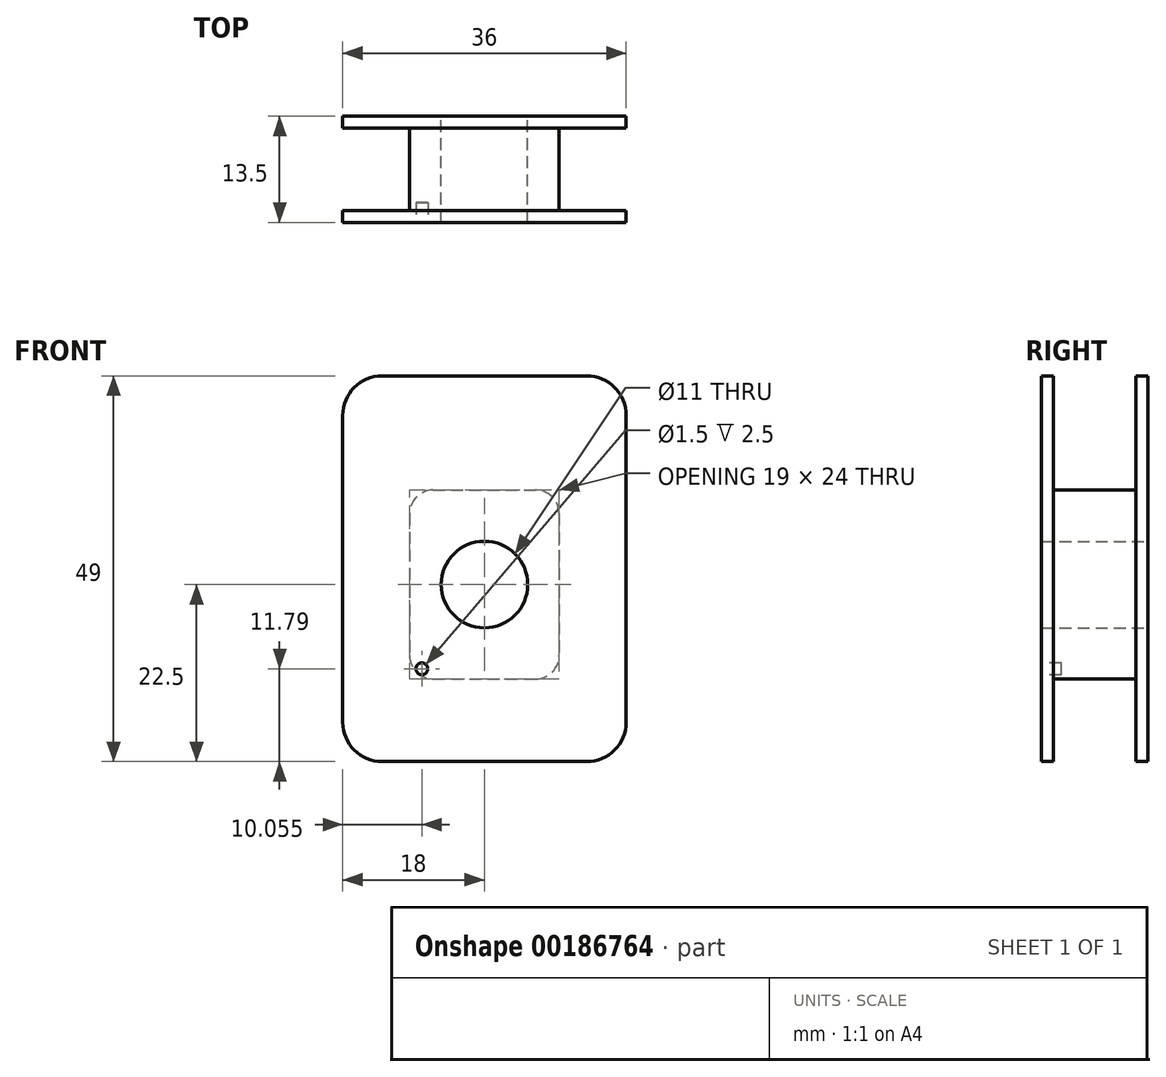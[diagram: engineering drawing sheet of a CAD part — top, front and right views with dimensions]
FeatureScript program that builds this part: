
annotation { "Feature Type Name" : "Feature", "Feature Type Description" : "" }
export const myFeature = defineFeature(function(context is Context, id is Id, definition is map)
    precondition{}
    {
        {
            var Q0;
            Q0=qCreatedBy(makeId("Front.planeOp"),FACE);
            var sketch = newSketch(context, id + "F0", { "sketchPlane" : qUnion([Q0])});
            skLineSegment(sketch, "E0.bottom", {"start": v(-18, 22.5) * mm, "end": v(18, 22.5) * mm});
            skLineSegment(sketch, "E0.top", {"start": v(-18, -22.5) * mm, "end": v(18, -22.5) * mm});
            skLineSegment(sketch, "E0.left", {"start": v(-18, 22.5) * mm, "end": v(-18, -22.5) * mm});
            skLineSegment(sketch, "E0.right", {"start": v(18, 22.5) * mm, "end": v(18, -22.5) * mm});
            skPoint(sketch, "E0.middle", {"position": v(0, 0) * mm});
            skCircle(sketch, "E1", {"center": v(0, 0) * mm, "radius": 5.5 * mm});
            skSolve(sketch);
        }
        {
            var Q0;
            Q0=makeQuery(id+"F0.imprint","IMPRINT",FACE,{"disambiguationData":[TD([[makeQuery(id+"F0.imprint","IMPRINT",EDGE,{"derivedFrom":sQuery(id+"F0.wireOp",EDGE,"E0.bottom")}),-1.0]])]});
            extrude(context, id + "F1", {"entities" : qUnion([Q0]), "depth" : 1.5 * mm});
        }
        {
            var Q0;
            Q0=makeQuery(id+"F1.opExtrude","CAP_FACE",FACE,{"disambiguationData":[OSD([sQuery(id+"F0.wireOp",EDGE,"E0.bottom"),sQuery(id+"F0.wireOp",EDGE,"E0.top"),sQuery(id+"F0.wireOp",EDGE,"E0.left"),sQuery(id+"F0.wireOp",EDGE,"E0.right"),sQuery(id+"F0.wireOp",EDGE,"E1")])],"isStart":false});
            var sketch = newSketch(context, id + "F2", { "sketchPlane" : qUnion([Q0])});
            skLineSegment(sketch, "E2.bottom", {"start": v(-9.5, 12) * mm, "end": v(9.5, 12) * mm});
            skLineSegment(sketch, "E2.top", {"start": v(-9.5, -12) * mm, "end": v(9.5, -12) * mm});
            skLineSegment(sketch, "E2.left", {"start": v(-9.5, 12) * mm, "end": v(-9.5, -12) * mm});
            skLineSegment(sketch, "E2.right", {"start": v(9.5, 12) * mm, "end": v(9.5, -12) * mm});
            skPoint(sketch, "E2.middle", {"position": v(0, 0) * mm});
            skSolve(sketch);
        }
        {
            var Q0;
            Q0=makeQuery(id+"F2.imprint","IMPRINT",FACE,{"disambiguationData":[TD([[makeQuery(id+"F2.imprint","IMPRINT",EDGE,{"derivedFrom":sQuery(id+"F2.wireOp",EDGE,"E2.bottom")}),-1.0]])]});
            extrude(context, id + "F3", {"entities" : qUnion([Q0]), "operationType" : NewBodyOperationType.ADD, "depth" : 12 * mm});
        }
        {
            var Q0;
            Q0=makeQuery(id+"F3.opExtrude","CAP_FACE",FACE,{"disambiguationData":[OSD([sQuery(id+"F0.wireOp",EDGE,"E1"),sQuery(id+"F2.wireOp",EDGE,"E2.bottom"),sQuery(id+"F2.wireOp",EDGE,"E2.top"),sQuery(id+"F2.wireOp",EDGE,"E2.left"),sQuery(id+"F2.wireOp",EDGE,"E2.right")])],"isStart":false});
            var sketch = newSketch(context, id + "F4", { "sketchPlane" : qUnion([Q0])});
            skLineSegment(sketch, "E3.bottom", {"start": v(-18, 22.5) * mm, "end": v(18, 22.5) * mm});
            skLineSegment(sketch, "E3.top", {"start": v(-18, -22.5) * mm, "end": v(18, -22.5) * mm});
            skLineSegment(sketch, "E3.left", {"start": v(-18, 22.5) * mm, "end": v(-18, -22.5) * mm});
            skLineSegment(sketch, "E3.right", {"start": v(18, 22.5) * mm, "end": v(18, -22.5) * mm});
            skPoint(sketch, "E3.middle", {"position": v(0, 0) * mm});
            skSolve(sketch);
        }
        {
            var Q0;
            Q0=makeQuery(id+"F4.imprint","IMPRINT",FACE,{"disambiguationData":[TD([[makeQuery(id+"F4.imprint","IMPRINT",EDGE,{"derivedFrom":sQuery(id+"F4.wireOp",EDGE,"E3.bottom")}),-1.0]])]});
            var Q1;
            Q1=makeQuery(id+"F4.imprint","IMPRINT",FACE,{"disambiguationData":[TD([[makeQuery(id+"F4.imprint","IMPRINT",EDGE,{"derivedFrom":makeQuery(id+"F3.opExtrude","CAP_EDGE",EDGE,{"disambiguationData":[OSD([sQuery(id+"F2.wireOp",EDGE,"E2.bottom")])],"isStart":false})}),-1.0]])]});
            extrude(context, id + "F5", {"entities" : qUnion([Q0, Q1]), "operationType" : NewBodyOperationType.ADD, "oppositeDirection" : true, "depth" : 1.5 * mm});
        }
        {
            var Q0;
            {var subQ0=sQuery(id+"F0.wireOp",EDGE,"E1");Q0=makeQuery(id+"F5.boolean.opBoolean","MERGE",FACE,{"derivedFrom":[makeQuery(id+"F3.opExtrude","CAP_FACE",FACE,{"disambiguationData":[OSD([subQ0,sQuery(id+"F2.wireOp",EDGE,"E2.bottom"),sQuery(id+"F2.wireOp",EDGE,"E2.top"),sQuery(id+"F2.wireOp",EDGE,"E2.left"),sQuery(id+"F2.wireOp",EDGE,"E2.right")])],"isStart":false}),makeQuery(id+"F5.opExtrude","CAP_FACE",FACE,{"disambiguationData":[OSD([subQ0,sQuery(id+"F4.wireOp",EDGE,"E3.bottom"),sQuery(id+"F4.wireOp",EDGE,"E3.top"),sQuery(id+"F4.wireOp",EDGE,"E3.left"),sQuery(id+"F4.wireOp",EDGE,"E3.right")])],"isStart":true})]});}
            var sketch = newSketch(context, id + "F6", { "sketchPlane" : qUnion([Q0])});
            skCircle(sketch, "E4", {"center": v(-7.94, -10.71) * mm, "radius": 0.75 * mm});
            skPoint(sketch, "E5.middle", {"position": v(0, 0) * mm});
            skSolve(sketch);
        }
        {
            var Q0;
            Q0=makeQuery(id+"F6.imprint","IMPRINT",FACE,{"disambiguationData":[TD([[makeQuery(id+"F6.imprint","IMPRINT",EDGE,{"derivedFrom":sQuery(id+"F6.wireOp",EDGE,"E4")}),1.0]])]});
            extrude(context, id + "F7", {"entities" : qUnion([Q0]), "operationType" : NewBodyOperationType.REMOVE, "oppositeDirection" : true, "depth" : 2.5 * mm});
        }
        {
            var Q0;
            {var subQ0=sQuery(id+"F0.wireOp",EDGE,"E1");Q0=makeQuery(id+"F5.boolean.opBoolean","MERGE",FACE,{"derivedFrom":[makeQuery(id+"F3.opExtrude","CAP_FACE",FACE,{"disambiguationData":[OSD([subQ0,sQuery(id+"F2.wireOp",EDGE,"E2.bottom"),sQuery(id+"F2.wireOp",EDGE,"E2.top"),sQuery(id+"F2.wireOp",EDGE,"E2.left"),sQuery(id+"F2.wireOp",EDGE,"E2.right")])],"isStart":false}),makeQuery(id+"F5.opExtrude","CAP_FACE",FACE,{"disambiguationData":[OSD([subQ0,sQuery(id+"F4.wireOp",EDGE,"E3.bottom"),sQuery(id+"F4.wireOp",EDGE,"E3.top"),sQuery(id+"F4.wireOp",EDGE,"E3.left"),sQuery(id+"F4.wireOp",EDGE,"E3.right")])],"isStart":true})]});}
            var sketch = newSketch(context, id + "F8", { "sketchPlane" : qUnion([Q0])});
            skLineSegment(sketch, "E6.bottom", {"start": v(-18, 22.5) * mm, "end": v(18, 22.5) * mm});
            skLineSegment(sketch, "E6.top", {"start": v(-18, 26.5) * mm, "end": v(18, 26.5) * mm});
            skLineSegment(sketch, "E6.left", {"start": v(-18, 22.5) * mm, "end": v(-18, 26.5) * mm});
            skLineSegment(sketch, "E6.right", {"start": v(18, 22.5) * mm, "end": v(18, 26.5) * mm});
            skSolve(sketch);
        }
        {
            var Q0;
            Q0=makeQuery(id+"F8.imprint","IMPRINT",FACE,{"disambiguationData":[TD([[makeQuery(id+"F8.imprint","IMPRINT",EDGE,{"derivedFrom":sQuery(id+"F8.wireOp",EDGE,"E6.bottom")}),1.0]])]});
            extrude(context, id + "F9", {"entities" : qUnion([Q0]), "operationType" : NewBodyOperationType.ADD, "oppositeDirection" : true, "depth" : 1.5 * mm});
        }
        {
            var Q0;
            Q0=makeQuery(id+"F1.opExtrude","CAP_FACE",FACE,{"disambiguationData":[OSD([sQuery(id+"F0.wireOp",EDGE,"E0.bottom"),sQuery(id+"F0.wireOp",EDGE,"E0.top"),sQuery(id+"F0.wireOp",EDGE,"E0.left"),sQuery(id+"F0.wireOp",EDGE,"E0.right"),sQuery(id+"F0.wireOp",EDGE,"E1")])],"isStart":true});
            var sketch = newSketch(context, id + "F10", { "sketchPlane" : qUnion([Q0])});
            skLineSegment(sketch, "E7.bottom", {"start": v(-18, 22.5) * mm, "end": v(18, 22.5) * mm});
            skLineSegment(sketch, "E7.top", {"start": v(-18, 26.5) * mm, "end": v(18, 26.5) * mm});
            skLineSegment(sketch, "E7.left", {"start": v(-18, 22.5) * mm, "end": v(-18, 26.5) * mm});
            skLineSegment(sketch, "E7.right", {"start": v(18, 22.5) * mm, "end": v(18, 26.5) * mm});
            skSolve(sketch);
        }
        {
            var Q0;
            Q0=makeQuery(id+"F10.imprint","IMPRINT",FACE,{"disambiguationData":[TD([[makeQuery(id+"F10.imprint","IMPRINT",EDGE,{"derivedFrom":sQuery(id+"F10.wireOp",EDGE,"E7.bottom")}),-1.0]])]});
            extrude(context, id + "F11", {"entities" : qUnion([Q0]), "operationType" : NewBodyOperationType.ADD, "oppositeDirection" : true, "depth" : 1.5 * mm});
        }
        {
            var Q0;
            Q0=makeQuery(id+"F9.opExtrude","SWEPT_EDGE",EDGE,{"disambiguationData":[OSD([sQuery(id+"F8.wireOp",EDGE,"E6.top"),sQuery(id+"F8.wireOp",EDGE,"E6.right")])]});
            var Q1;
            Q1=makeQuery(id+"F11.opExtrude","SWEPT_EDGE",EDGE,{"disambiguationData":[OSD([sQuery(id+"F10.wireOp",EDGE,"E7.top"),sQuery(id+"F10.wireOp",EDGE,"E7.left")])]});
            var Q2;
            Q2=makeQuery(id+"F1.opExtrude","SWEPT_EDGE",EDGE,{"disambiguationData":[OSD([sQuery(id+"F0.wireOp",EDGE,"E0.top"),sQuery(id+"F0.wireOp",EDGE,"E0.right")])]});
            var Q3;
            Q3=makeQuery(id+"F5.opExtrude","SWEPT_EDGE",EDGE,{"disambiguationData":[OSD([sQuery(id+"F4.wireOp",EDGE,"E3.top"),sQuery(id+"F4.wireOp",EDGE,"E3.right")])]});
            var Q4;
            Q4=makeQuery(id+"F1.opExtrude","SWEPT_EDGE",EDGE,{"disambiguationData":[OSD([sQuery(id+"F0.wireOp",EDGE,"E0.top"),sQuery(id+"F0.wireOp",EDGE,"E0.left")])]});
            var Q5;
            Q5=makeQuery(id+"F5.opExtrude","SWEPT_EDGE",EDGE,{"disambiguationData":[OSD([sQuery(id+"F4.wireOp",EDGE,"E3.top"),sQuery(id+"F4.wireOp",EDGE,"E3.left")])]});
            var Q6;
            Q6=makeQuery(id+"F11.opExtrude","SWEPT_EDGE",EDGE,{"disambiguationData":[OSD([sQuery(id+"F10.wireOp",EDGE,"E7.top"),sQuery(id+"F10.wireOp",EDGE,"E7.right")])]});
            var Q7;
            Q7=makeQuery(id+"F9.opExtrude","SWEPT_EDGE",EDGE,{"disambiguationData":[OSD([sQuery(id+"F8.wireOp",EDGE,"E6.top"),sQuery(id+"F8.wireOp",EDGE,"E6.left")])]});
            fillet(context, id + "F12", {"entities" : qUnion([Q0, Q1, Q2, Q3, Q4, Q5, Q6, Q7]), "radius" : 5 * mm, "tangentPropagation" : true, "allowEdgeOverflow" : false});
        }
        {
            var Q0;
            Q0=makeQuery(id+"F3.opExtrude","SWEPT_EDGE",EDGE,{"disambiguationData":[OSD([sQuery(id+"F2.wireOp",EDGE,"E2.bottom"),sQuery(id+"F2.wireOp",EDGE,"E2.left")])]});
            var Q1;
            Q1=makeQuery(id+"F3.opExtrude","SWEPT_EDGE",EDGE,{"disambiguationData":[OSD([sQuery(id+"F2.wireOp",EDGE,"E2.bottom"),sQuery(id+"F2.wireOp",EDGE,"E2.right")])]});
            var Q2;
            Q2=makeQuery(id+"F3.opExtrude","SWEPT_EDGE",EDGE,{"disambiguationData":[OSD([sQuery(id+"F2.wireOp",EDGE,"E2.top"),sQuery(id+"F2.wireOp",EDGE,"E2.right")])]});
            var Q3;
            Q3=makeQuery(id+"F3.opExtrude","SWEPT_EDGE",EDGE,{"disambiguationData":[OSD([sQuery(id+"F2.wireOp",EDGE,"E2.top"),sQuery(id+"F2.wireOp",EDGE,"E2.left")])]});
            fillet(context, id + "F13", {"entities" : qUnion([Q0, Q1, Q2, Q3]), "radius" : 3 * mm, "tangentPropagation" : true, "allowEdgeOverflow" : false});
        }
    });
